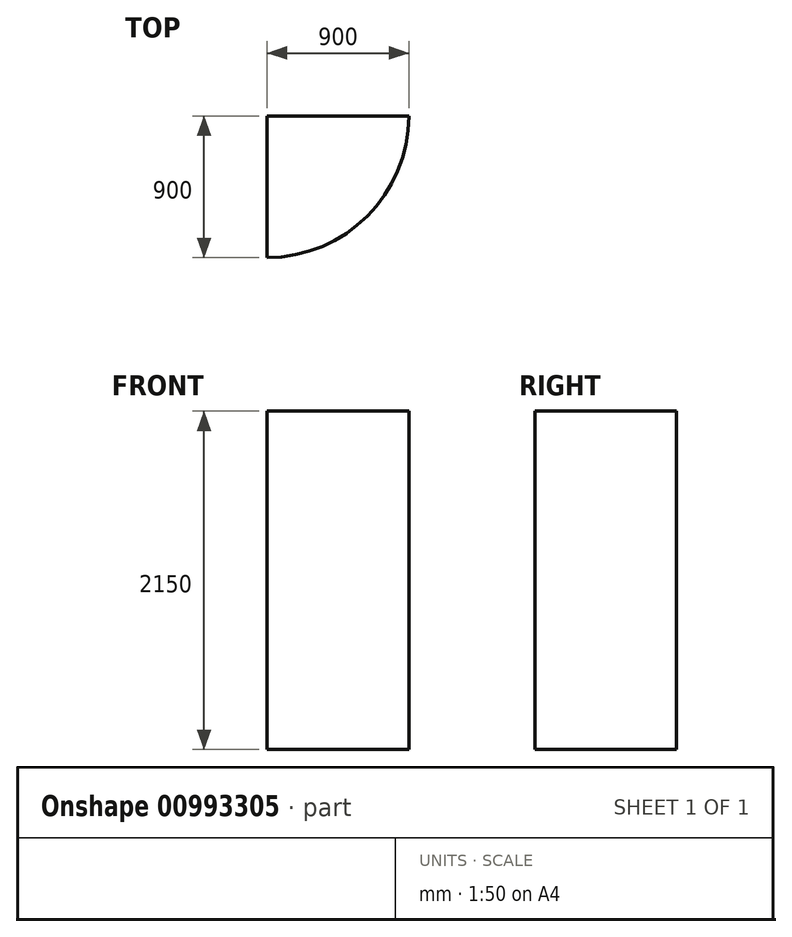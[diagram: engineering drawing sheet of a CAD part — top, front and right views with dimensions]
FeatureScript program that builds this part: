
annotation { "Feature Type Name" : "Feature", "Feature Type Description" : "" }
export const myFeature = defineFeature(function(context is Context, id is Id, definition is map)
    precondition{}
    {
        {
            var Q0;
            Q0=qCreatedBy(makeId("Top.planeOp"),FACE);
            var sketch = newSketch(context, id + "F0", { "sketchPlane" : qUnion([Q0])});
            skLineSegment(sketch, "E0", {"start": v(0, 0) * mm, "end": v(900, 0) * mm});
            skLineSegment(sketch, "E1", {"start": v(0, 0) * mm, "end": v(0, -900) * mm});
            skArc(sketch, "E2", {"start": v(0, -900) * mm, "mid": v(636.4, -636.4) * mm, "end": v(900, 0) * mm});
            skSolve(sketch);
        }
        {
            var Q0;
            Q0=makeQuery(id+"F0.imprint","IMPRINT",FACE,{"disambiguationData":[TD([[makeQuery(id+"F0.imprint","IMPRINT",EDGE,{"derivedFrom":sQuery(id+"F0.wireOp",EDGE,"E0")}),-1.0]])]});
            extrude(context, id + "F1", {"entities" : qUnion([Q0]), "depth" : 2150 * mm, "offsetDistance" : 25 * mm});
        }
    });
